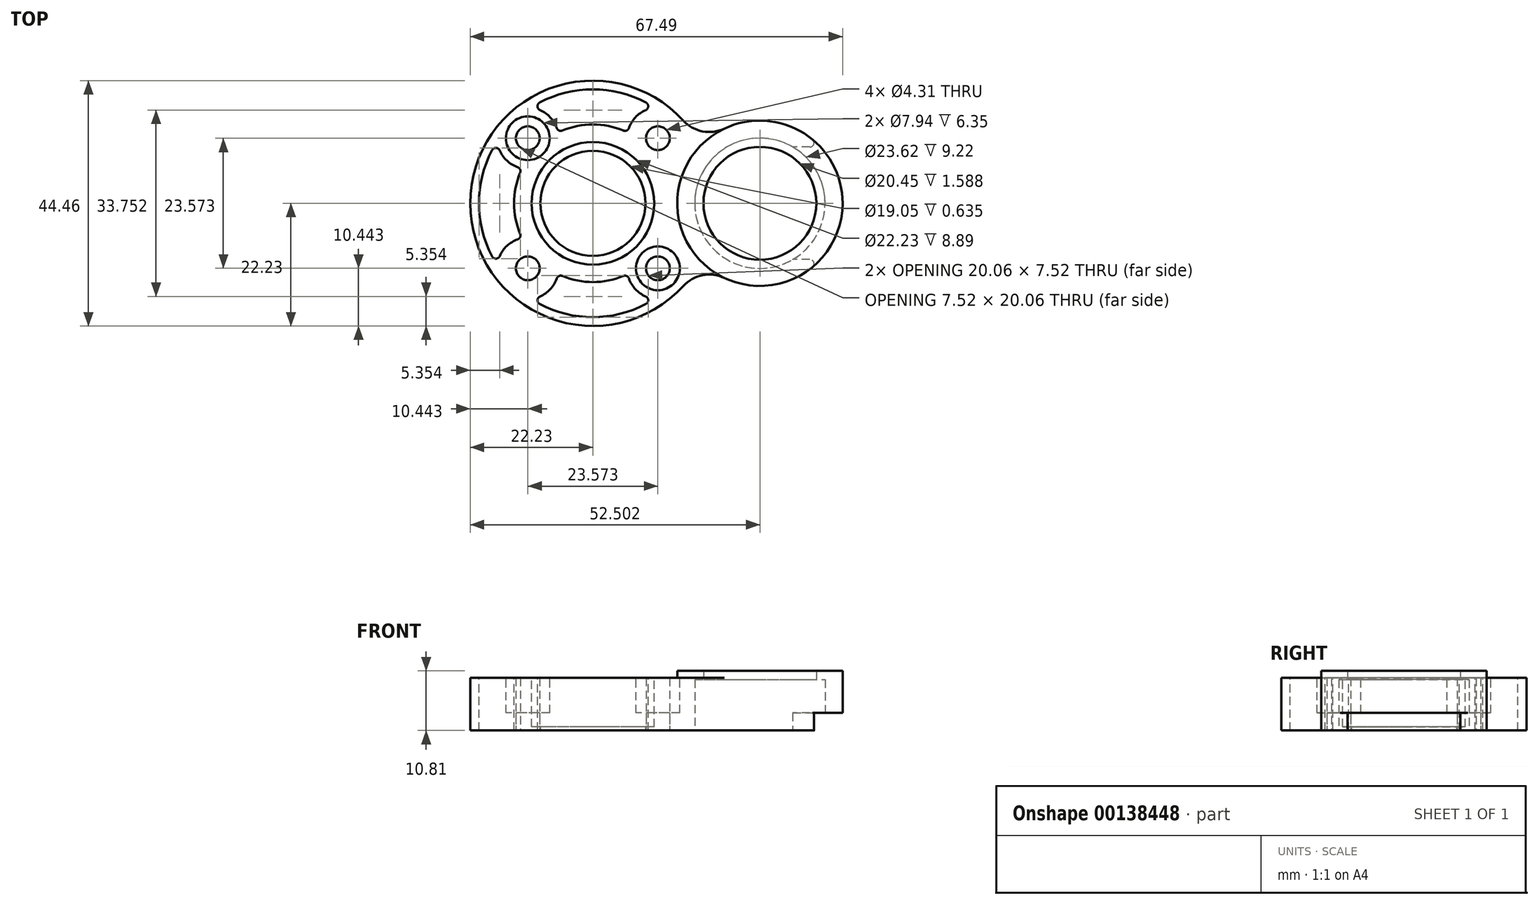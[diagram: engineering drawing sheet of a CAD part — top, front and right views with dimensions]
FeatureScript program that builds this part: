
annotation { "Feature Type Name" : "Feature", "Feature Type Description" : "" }
export const myFeature = defineFeature(function(context is Context, id is Id, definition is map)
    precondition{}
    {
        {
            var Q0;
            Q0=qCreatedBy(makeId("Top.planeOp"),FACE);
            var sketch = newSketch(context, id + "F0", { "sketchPlane" : qUnion([Q0])});
            skCircle(sketch, "E0", {"center": v(0, 0) * mm, "radius": 9.53 * mm});
            skLineSegment(sketch, "E1.bottom", {"start": v(-11.79, 11.79) * mm, "end": v(11.79, 11.79) * mm, "construction": true});
            skLineSegment(sketch, "E1.top", {"start": v(-11.79, -11.79) * mm, "end": v(11.79, -11.79) * mm, "construction": true});
            skLineSegment(sketch, "E1.left", {"start": v(-11.79, 11.79) * mm, "end": v(-11.79, -11.79) * mm, "construction": true});
            skLineSegment(sketch, "E1.right", {"start": v(11.79, 11.79) * mm, "end": v(11.79, -11.79) * mm, "construction": true});
            skCircle(sketch, "E2", {"center": v(0, 0) * mm, "radius": 11.11 * mm, "construction": true});
            skCircle(sketch, "E3", {"center": v(-11.79, 11.79) * mm, "radius": 5.56 * mm, "construction": true});
            skCircle(sketch, "E4", {"center": v(-11.79, 11.79) * mm, "radius": 2.15 * mm});
            skCircle(sketch, "E5", {"center": v(11.79, 11.79) * mm, "radius": 2.15 * mm});
            skCircle(sketch, "E6", {"center": v(-11.79, -11.79) * mm, "radius": 2.15 * mm});
            skCircle(sketch, "E7", {"center": v(11.79, -11.79) * mm, "radius": 2.15 * mm});
            skLineSegment(sketch, "E8", {"start": v(0, 0) * mm, "end": v(30.27, 0) * mm, "construction": true});
            skCircle(sketch, "E9", {"center": v(30.27, 0) * mm, "radius": 10.22 * mm});
            skArc(sketch, "E10", {"start": v(19.59, 10.5) * mm, "mid": v(-22.22, 0) * mm, "end": v(19.59, -10.5) * mm});
            skArc(sketch, "E11", {"start": v(19.59, -10.5) * mm, "mid": v(45.26, 0) * mm, "end": v(19.59, 10.5) * mm});
            skSolve(sketch);
        }
        {
            var Q0;
            Q0=qSketchRegion(id+"F0",true);
            extrude(context, id + "F1", {"entities" : qUnion([Q0]), "depth" : 9.52 * mm});
        }
        {
            var Q0;
            Q0=makeQuery(id+"F1.opExtrude","CAP_FACE",FACE,{"disambiguationData":[OSD([sQuery(id+"F0.wireOp",EDGE,"E0"),sQuery(id+"F0.wireOp",EDGE,"E4"),sQuery(id+"F0.wireOp",EDGE,"E5"),sQuery(id+"F0.wireOp",EDGE,"E6"),sQuery(id+"F0.wireOp",EDGE,"E7"),sQuery(id+"F0.wireOp",EDGE,"zBUUjadT-Mwnb-Mu9x-voaD-4Vu0ZQ8WAPE4")])],"isStart":false});
            var sketch = newSketch(context, id + "F2", { "sketchPlane" : qUnion([Q0])});
            skCircle(sketch, "E12", {"center": v(-11.79, 11.79) * mm, "radius": 3.97 * mm});
            skCircle(sketch, "E13", {"center": v(11.79, -11.79) * mm, "radius": 3.97 * mm});
            skSolve(sketch);
        }
        {
            var Q0;
            Q0=qSketchRegion(id+"F2",true);
            extrude(context, id + "F3", {"entities" : qUnion([Q0]), "operationType" : NewBodyOperationType.REMOVE, "oppositeDirection" : true, "depth" : 6.35 * mm});
        }
        {
            var Q0;
            Q0=makeQuery(id+"F1.opExtrude","CAP_FACE",FACE,{"disambiguationData":[OSD([sQuery(id+"F0.wireOp",EDGE,"E0"),sQuery(id+"F0.wireOp",EDGE,"E4"),sQuery(id+"F0.wireOp",EDGE,"E5"),sQuery(id+"F0.wireOp",EDGE,"E6"),sQuery(id+"F0.wireOp",EDGE,"E7"),sQuery(id+"F0.wireOp",EDGE,"zBUUjadT-Mwnb-Mu9x-voaD-4Vu0ZQ8WAPE4")])],"isStart":false});
            var sketch = newSketch(context, id + "F4", { "sketchPlane" : qUnion([Q0])});
            skCircle(sketch, "E14", {"center": v(0, 0) * mm, "radius": 11.11 * mm});
            skSolve(sketch);
        }
        {
            var Q0;
            Q0 = qSketchRegion(id + "F4", true);
            extrude(context, id + "F5", {"entities" : qUnion([Q0]), "operationType" : NewBodyOperationType.REMOVE, "oppositeDirection" : true, "depth" : 8.9 * mm});
        }
        {
            var Q0;
            {var subQ0=sQuery(id+"F0.wireOp",EDGE,"E11");var subQ1=sQuery(id+"F0.wireOp",EDGE,"E10");Q0=makeQuery(id+"F1.opExtrude","SWEPT_EDGE",EDGE,{"disambiguationData":[OSD([subQ1,subQ0]),TDD([makeQuery(id+"F0.imprint","INTERSECT",VERTEX,{"disambiguationData":[OD(1.0)],"derivedFrom":[subQ1,subQ0]})])]});}
            var Q1;
            {var subQ0=sQuery(id+"F0.wireOp",EDGE,"E11");var subQ1=sQuery(id+"F0.wireOp",EDGE,"E10");Q1=makeQuery(id+"F1.opExtrude","SWEPT_EDGE",EDGE,{"disambiguationData":[OSD([subQ1,subQ0]),TDD([makeQuery(id+"F0.imprint","INTERSECT",VERTEX,{"disambiguationData":[OD(0.0)],"derivedFrom":[subQ1,subQ0]})])]});}
            fillet(context, id + "F6", {"entities" : qUnion([Q0, Q1]), "radius" : 6.35 * mm, "tangentPropagation" : true, "allowEdgeOverflow" : false});
        }
        {
            var Q0;
            Q0=makeQuery(id+"F1.opExtrude","CAP_FACE",FACE,{"disambiguationData":[OSD([sQuery(id+"F0.wireOp",EDGE,"E0"),sQuery(id+"F0.wireOp",EDGE,"E4"),sQuery(id+"F0.wireOp",EDGE,"E5"),sQuery(id+"F0.wireOp",EDGE,"E6"),sQuery(id+"F0.wireOp",EDGE,"E7"),sQuery(id+"F0.wireOp",EDGE,"E9"),sQuery(id+"F0.wireOp",EDGE,"E10"),sQuery(id+"F0.wireOp",EDGE,"E11")])],"isStart":false});
            var sketch = newSketch(context, id + "F7", { "sketchPlane" : qUnion([Q0])});
            skCircle(sketch, "E15", {"center": v(30.27, 0) * mm, "radius": 10.22 * mm});
            skCircle(sketch, "E16", {"center": v(30.27, 0) * mm, "radius": 14.99 * mm});
            skSolve(sketch);
        }
        {
            var Q0;
            Q0 = qSketchRegion(id + "F7", true);
            extrude(context, id + "F8", {"entities" : qUnion([Q0]), "operationType" : NewBodyOperationType.ADD, "depth" : 1.28 * mm});
        }
        {
            var Q0;
            Q0=makeQuery(id+"F1.opExtrude","CAP_FACE",FACE,{"disambiguationData":[OSD([sQuery(id+"F0.wireOp",EDGE,"E0"),sQuery(id+"F0.wireOp",EDGE,"E4"),sQuery(id+"F0.wireOp",EDGE,"E5"),sQuery(id+"F0.wireOp",EDGE,"E6"),sQuery(id+"F0.wireOp",EDGE,"E7"),sQuery(id+"F0.wireOp",EDGE,"E9"),sQuery(id+"F0.wireOp",EDGE,"E10"),sQuery(id+"F0.wireOp",EDGE,"E11")])],"isStart":true});
            var sketch = newSketch(context, id + "F9", { "sketchPlane" : qUnion([Q0])});
            skCircle(sketch, "E17", {"center": v(30.27, 0) * mm, "radius": 11.81 * mm});
            skSolve(sketch);
        }
        {
            var Q0;
            Q0 = qSketchRegion(id + "F9", true);
            extrude(context, id + "F10", {"entities" : qUnion([Q0]), "operationType" : NewBodyOperationType.REMOVE, "oppositeDirection" : true, "depth" : 9.22 * mm});
        }
        {
            var Q0;
            Q0=makeQuery(id+"F1.opExtrude","CAP_FACE",FACE,{"disambiguationData":[OSD([sQuery(id+"F0.wireOp",EDGE,"E0"),sQuery(id+"F0.wireOp",EDGE,"E4"),sQuery(id+"F0.wireOp",EDGE,"E5"),sQuery(id+"F0.wireOp",EDGE,"E6"),sQuery(id+"F0.wireOp",EDGE,"E7"),sQuery(id+"F0.wireOp",EDGE,"E9"),sQuery(id+"F0.wireOp",EDGE,"E10"),sQuery(id+"F0.wireOp",EDGE,"E11")])],"isStart":true});
            var sketch = newSketch(context, id + "F11", { "sketchPlane" : qUnion([Q0])});
            skLineSegment(sketch, "E18.bottom", {"start": v(45.26, -10.2) * mm, "end": v(36.23, -10.2) * mm});
            skLineSegment(sketch, "E18.top", {"start": v(45.26, 10.2) * mm, "end": v(36.23, 10.2) * mm});
            skLineSegment(sketch, "E18.left", {"start": v(45.26, -10.2) * mm, "end": v(45.26, 10.2) * mm});
            skLineSegment(sketch, "E18.right", {"start": v(36.23, -10.2) * mm, "end": v(36.23, 10.2) * mm});
            skSolve(sketch);
        }
        {
            var Q0;
            Q0 = qSketchRegion(id + "F11", true);
            extrude(context, id + "F12", {"entities" : qUnion([Q0]), "operationType" : NewBodyOperationType.REMOVE, "oppositeDirection" : true, "depth" : 3.17 * mm});
        }
        {
            var Q0;
            Q0=makeQuery(id+"F12.boolean.opBoolean","INTERSECT",EDGE,{"derivedFrom":[makeQuery(id+"F8.boolean.opBoolean","MERGE",FACE,{"derivedFrom":[makeQuery(id+"F1.opExtrude","SWEPT_FACE",FACE,{"disambiguationData":[OSD([sQuery(id+"F0.wireOp",EDGE,"E11")])]}),makeQuery(id+"F8.opExtrude","SWEPT_FACE",FACE,{"disambiguationData":[OSD([sQuery(id+"F7.wireOp",EDGE,"E16")])]})]}),makeQuery(id+"F12.opExtrude","SWEPT_FACE",FACE,{"disambiguationData":[OSD([sQuery(id+"F11.wireOp",EDGE,"E18.bottom")])]})]});
            var Q1;
            Q1=makeQuery(id+"F12.boolean.opBoolean","INTERSECT",EDGE,{"derivedFrom":[makeQuery(id+"F8.boolean.opBoolean","MERGE",FACE,{"derivedFrom":[makeQuery(id+"F1.opExtrude","SWEPT_FACE",FACE,{"disambiguationData":[OSD([sQuery(id+"F0.wireOp",EDGE,"E11")])]}),makeQuery(id+"F8.opExtrude","SWEPT_FACE",FACE,{"disambiguationData":[OSD([sQuery(id+"F7.wireOp",EDGE,"E16")])]})]}),makeQuery(id+"F12.opExtrude","SWEPT_FACE",FACE,{"disambiguationData":[OSD([sQuery(id+"F11.wireOp",EDGE,"E18.top")])]})]});
            fillet(context, id + "F13", {"entities" : qUnion([Q0, Q1]), "radius" : 0.76 * mm, "tangentPropagation" : true, "allowEdgeOverflow" : false});
        }
        {
            var Q0;
            Q0=makeQuery(id+"F1.opExtrude","CAP_FACE",FACE,{"disambiguationData":[OSD([sQuery(id+"F0.wireOp",EDGE,"E0"),sQuery(id+"F0.wireOp",EDGE,"E4"),sQuery(id+"F0.wireOp",EDGE,"E5"),sQuery(id+"F0.wireOp",EDGE,"E6"),sQuery(id+"F0.wireOp",EDGE,"E7"),sQuery(id+"F0.wireOp",EDGE,"E9"),sQuery(id+"F0.wireOp",EDGE,"E10"),sQuery(id+"F0.wireOp",EDGE,"E11")])],"isStart":false});
            var sketch = newSketch(context, id + "F14", { "sketchPlane" : qUnion([Q0])});
            skArc(sketch, "E19", {"start": v(6.33, -12.81) * mm, "mid": v(8.03, -15.88) * mm, "end": v(11.23, -17.31) * mm});
            skArc(sketch, "E20", {"start": v(-6.33, -12.81) * mm, "mid": v(0, -14.29) * mm, "end": v(6.33, -12.81) * mm});
            skArc(sketch, "E21", {"start": v(-11.23, -17.31) * mm, "mid": v(-8.03, -15.88) * mm, "end": v(-6.33, -12.81) * mm});
            skArc(sketch, "E22", {"start": v(-11.23, -17.31) * mm, "mid": v(0, -20.64) * mm, "end": v(11.23, -17.31) * mm});
            skSolve(sketch);
        }
        {
            var Q0;
            Q0 = qSketchRegion(id + "F14", true);
            var Q1;
            Q1=makeQuery(id+"F1.opExtrude","CAP_FACE",FACE,{"disambiguationData":[OSD([sQuery(id+"F0.wireOp",EDGE,"E0"),sQuery(id+"F0.wireOp",EDGE,"E4"),sQuery(id+"F0.wireOp",EDGE,"E5"),sQuery(id+"F0.wireOp",EDGE,"E6"),sQuery(id+"F0.wireOp",EDGE,"E7"),sQuery(id+"F0.wireOp",EDGE,"E9"),sQuery(id+"F0.wireOp",EDGE,"E10"),sQuery(id+"F0.wireOp",EDGE,"E11")])],"isStart":true});
            extrude(context, id + "F15", {"entities" : qUnion([Q0]), "operationType" : NewBodyOperationType.REMOVE, "endBound" : BoundingType.UP_TO_SURFACE, "oppositeDirection" : true, "endBoundEntityFace" : qUnion([Q1]), "depth" : 25.4 * mm});
        }
        {
            var Q0;
            Q0=makeQuery(id+"F15.boolean.opBoolean","COPY",EDGE,{"derivedFrom":makeQuery(id+"F15.opExtrude","SWEPT_EDGE",EDGE,{"disambiguationData":[OSD([sQuery(id+"F14.wireOp",EDGE,"E21"),sQuery(id+"F14.wireOp",EDGE,"E22")])]})});
            var Q1;
            Q1=makeQuery(id+"F15.boolean.opBoolean","COPY",EDGE,{"derivedFrom":makeQuery(id+"F15.opExtrude","SWEPT_EDGE",EDGE,{"disambiguationData":[OSD([sQuery(id+"F14.wireOp",EDGE,"E20"),sQuery(id+"F14.wireOp",EDGE,"E21")])]})});
            var Q2;
            Q2=makeQuery(id+"F15.boolean.opBoolean","COPY",EDGE,{"derivedFrom":makeQuery(id+"F15.opExtrude","SWEPT_EDGE",EDGE,{"disambiguationData":[OSD([sQuery(id+"F14.wireOp",EDGE,"E19"),sQuery(id+"F14.wireOp",EDGE,"E20")])]})});
            var Q3;
            Q3=makeQuery(id+"F15.boolean.opBoolean","COPY",EDGE,{"derivedFrom":makeQuery(id+"F15.opExtrude","SWEPT_EDGE",EDGE,{"disambiguationData":[OSD([sQuery(id+"F14.wireOp",EDGE,"E19"),sQuery(id+"F14.wireOp",EDGE,"E22")])]})});
            fillet(context, id + "F16", {"entities" : qUnion([Q0, Q1, Q2, Q3]), "radius" : 0.76 * mm, "tangentPropagation" : true, "allowEdgeOverflow" : false});
        }
        {
            var Q0;
            Q0=makeQuery(id+"F16.opFillet","BLEND_FACE",FACE,{"disambiguationData":[OSD([sQuery(id+"F14.wireOp",EDGE,"E19"),sQuery(id+"F14.wireOp",EDGE,"E22")])]});
            var Q1;
            Q1=makeQuery(id+"F15.boolean.opBoolean","COPY",FACE,{"derivedFrom":makeQuery(id+"F15.opExtrude","SWEPT_FACE",FACE,{"disambiguationData":[OSD([sQuery(id+"F14.wireOp",EDGE,"E22")])]})});
            var Q2;
            Q2=makeQuery(id+"F15.boolean.opBoolean","COPY",FACE,{"derivedFrom":makeQuery(id+"F15.opExtrude","SWEPT_FACE",FACE,{"disambiguationData":[OSD([sQuery(id+"F14.wireOp",EDGE,"E19")])]})});
            var Q3;
            Q3=makeQuery(id+"F16.opFillet","BLEND_FACE",FACE,{"disambiguationData":[OSD([sQuery(id+"F14.wireOp",EDGE,"E19"),sQuery(id+"F14.wireOp",EDGE,"E20")])]});
            var Q4;
            Q4=makeQuery(id+"F15.boolean.opBoolean","COPY",FACE,{"derivedFrom":makeQuery(id+"F15.opExtrude","SWEPT_FACE",FACE,{"disambiguationData":[OSD([sQuery(id+"F14.wireOp",EDGE,"E20")])]})});
            var Q5;
            Q5=makeQuery(id+"F16.opFillet","BLEND_FACE",FACE,{"disambiguationData":[OSD([sQuery(id+"F14.wireOp",EDGE,"E20"),sQuery(id+"F14.wireOp",EDGE,"E21")])]});
            var Q6;
            Q6=makeQuery(id+"F15.boolean.opBoolean","COPY",FACE,{"derivedFrom":makeQuery(id+"F15.opExtrude","SWEPT_FACE",FACE,{"disambiguationData":[OSD([sQuery(id+"F14.wireOp",EDGE,"E21")])]})});
            var Q7;
            Q7=makeQuery(id+"F16.opFillet","BLEND_FACE",FACE,{"disambiguationData":[OSD([sQuery(id+"F14.wireOp",EDGE,"E21"),sQuery(id+"F14.wireOp",EDGE,"E22")])]});
            var Q8;
            Q8=makeQuery(id+"F1.opExtrude","SWEPT_FACE",FACE,{"disambiguationData":[OSD([sQuery(id+"F0.wireOp",EDGE,"E10")])]});
            circularPattern(context, id + "F17", {"patternType" : PatternType.FACE, "faces" : qUnion([Q0, Q1, Q2, Q3, Q4, Q5, Q6, Q7]), "axis" : qUnion([Q8]), "angle" : 90 * degree, "instanceCount" : 3});
        }
    });
